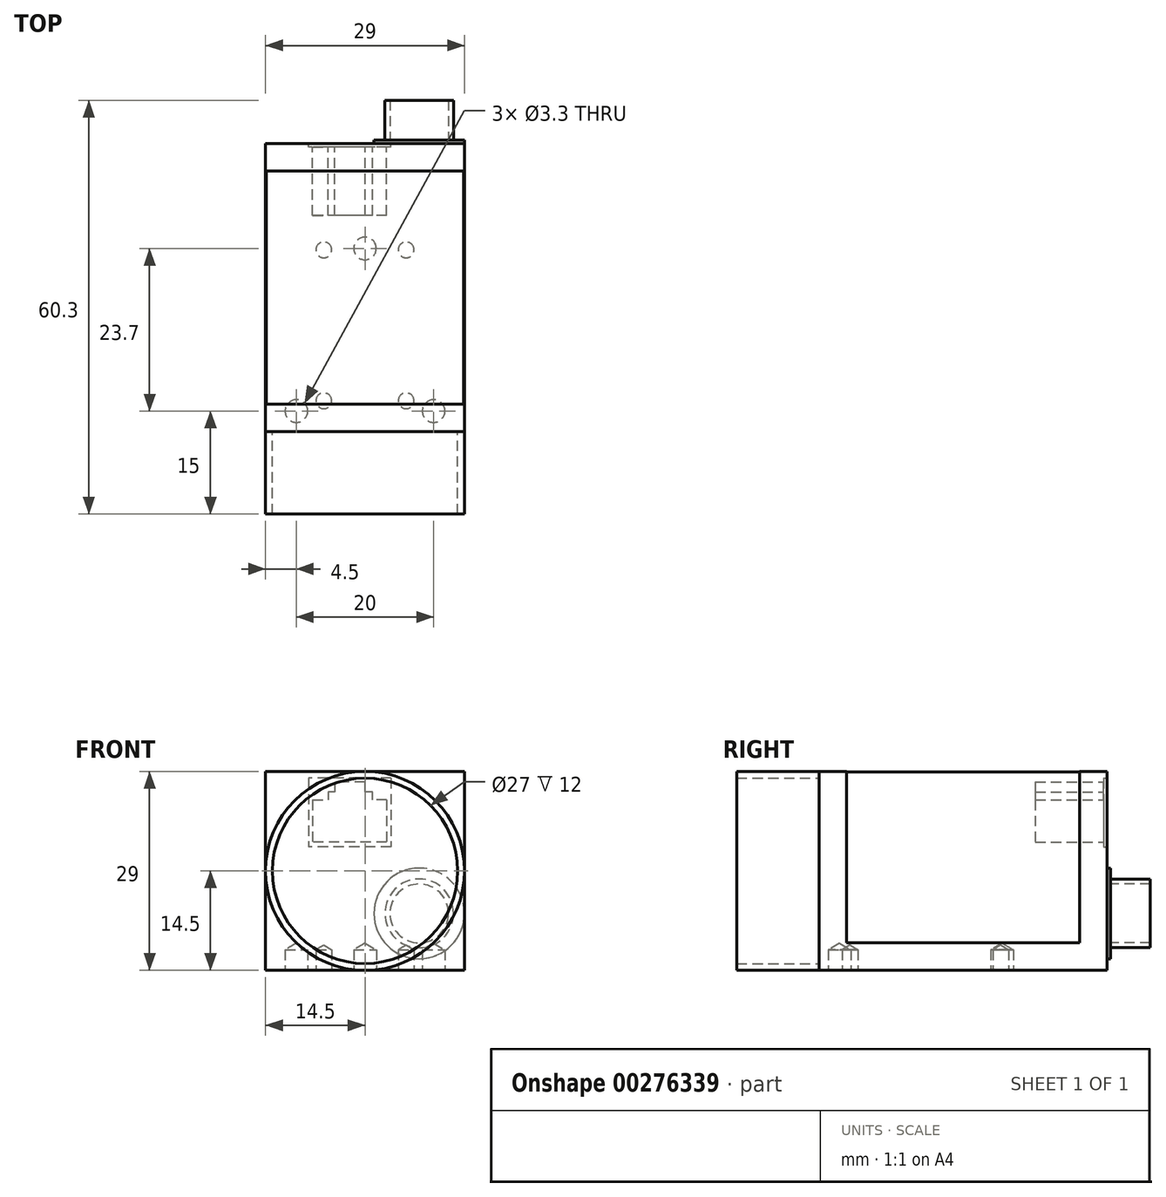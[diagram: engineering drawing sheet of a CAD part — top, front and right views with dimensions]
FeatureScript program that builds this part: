
annotation { "Feature Type Name" : "Feature", "Feature Type Description" : "" }
export const myFeature = defineFeature(function(context is Context, id is Id, definition is map)
    precondition{}
    {
        {
            var Q0;
            Q0=qCreatedBy(makeId("Front.planeOp"),FACE);
            var sketch = newSketch(context, id + "F0", { "sketchPlane" : qUnion([Q0])});
            skLineSegment(sketch, "E0.bottom", {"start": v(-14.5, 14.5) * mm, "end": v(14.5, 14.5) * mm});
            skLineSegment(sketch, "E0.top", {"start": v(-14.5, -14.5) * mm, "end": v(14.5, -14.5) * mm});
            skLineSegment(sketch, "E0.left", {"start": v(-14.5, 14.5) * mm, "end": v(-14.5, -14.5) * mm});
            skLineSegment(sketch, "E0.right", {"start": v(14.5, 14.5) * mm, "end": v(14.5, -14.5) * mm});
            skPoint(sketch, "E0.middle", {"position": v(0, 0) * mm});
            skSolve(sketch);
        }
        {
            var Q0;
            Q0 = qSketchRegion(id + "F0", true);
            extrude(context, id + "F1", {"entities" : qUnion([Q0]), "depth" : 42 * mm});
        }
        {
            var Q0;
            Q0=makeQuery(id+"F1.opExtrude","CAP_FACE",FACE,{"disambiguationData":[OSD([sQuery(id+"F0.wireOp",EDGE,"E0.bottom"),sQuery(id+"F0.wireOp",EDGE,"E0.top"),sQuery(id+"F0.wireOp",EDGE,"E0.left"),sQuery(id+"F0.wireOp",EDGE,"E0.right")])],"isStart":false});
            var sketch = newSketch(context, id + "F2", { "sketchPlane" : qUnion([Q0])});
            skCircle(sketch, "E1", {"center": v(0, 0) * mm, "radius": 14.5 * mm});
            skCircle(sketch, "E2", {"center": v(0, 0) * mm, "radius": 13.5 * mm});
            skSolve(sketch);
        }
        {
            var Q0;
            Q0 = qSketchRegion(id + "F2", true);
            extrude(context, id + "F3", {"entities" : qUnion([Q0]), "operationType" : NewBodyOperationType.ADD, "depth" : 12 * mm});
        }
        {
            var Q0;
            Q0=makeQuery(id+"F1.opExtrude","SWEPT_FACE",FACE,{"disambiguationData":[OSD([sQuery(id+"F0.wireOp",EDGE,"E0.right")])]});
            var sketch = newSketch(context, id + "F4", { "sketchPlane" : qUnion([Q0])});
            skLineSegment(sketch, "E3.bottom", {"start": v(-38, 14.5) * mm, "end": v(-4, 14.5) * mm});
            skLineSegment(sketch, "E3.top", {"start": v(-38, -10.5) * mm, "end": v(-4, -10.5) * mm});
            skLineSegment(sketch, "E3.left", {"start": v(-38, 14.5) * mm, "end": v(-38, -10.5) * mm});
            skLineSegment(sketch, "E3.right", {"start": v(-4, 14.5) * mm, "end": v(-4, -10.5) * mm});
            skSolve(sketch);
        }
        {
            var Q0;
            Q0 = qSketchRegion(id + "F4", true);
            extrude(context, id + "F5", {"entities" : qUnion([Q0]), "operationType" : NewBodyOperationType.REMOVE, "oppositeDirection" : true, "depth" : 0.1 * mm});
        }
        {
            var Q0;
            Q0=makeQuery(id+"F1.opExtrude","SWEPT_FACE",FACE,{"disambiguationData":[OSD([sQuery(id+"F0.wireOp",EDGE,"E0.left")])]});
            var sketch = newSketch(context, id + "F6", { "sketchPlane" : qUnion([Q0])});
            skLineSegment(sketch, "E4.bottom", {"start": v(4, -10.5) * mm, "end": v(38, -10.5) * mm});
            skLineSegment(sketch, "E4.top", {"start": v(4, 14.5) * mm, "end": v(38, 14.5) * mm});
            skLineSegment(sketch, "E4.left", {"start": v(4, -10.5) * mm, "end": v(4, 14.5) * mm});
            skLineSegment(sketch, "E4.right", {"start": v(38, -10.5) * mm, "end": v(38, 14.5) * mm});
            skSolve(sketch);
        }
        {
            var Q0;
            Q0=makeQuery(id+"F6.imprint","IMPRINT",FACE,{"disambiguationData":[TD([[makeQuery(id+"F6.imprint","IMPRINT",EDGE,{"derivedFrom":sQuery(id+"F6.wireOp",EDGE,"E4.bottom")}),1.0]])]});
            extrude(context, id + "F7", {"entities" : qUnion([Q0]), "operationType" : NewBodyOperationType.REMOVE, "oppositeDirection" : true, "depth" : 0.1 * mm});
        }
        {
            var Q0;
            Q0=makeQuery(id+"F1.opExtrude","SWEPT_FACE",FACE,{"disambiguationData":[OSD([sQuery(id+"F0.wireOp",EDGE,"E0.bottom")])]});
            var sketch = newSketch(context, id + "F8", { "sketchPlane" : qUnion([Q0])});
            skLineSegment(sketch, "E5.bottom", {"start": v(14.5, -4) * mm, "end": v(-14.4, -4) * mm});
            skLineSegment(sketch, "E5.top", {"start": v(14.5, -38) * mm, "end": v(-14.4, -38) * mm});
            skLineSegment(sketch, "E5.left", {"start": v(14.5, -4) * mm, "end": v(14.5, -38) * mm});
            skLineSegment(sketch, "E5.right", {"start": v(-14.4, -4) * mm, "end": v(-14.4, -38) * mm});
            skSolve(sketch);
        }
        {
            var Q0;
            Q0 = qSketchRegion(id + "F8", true);
            extrude(context, id + "F9", {"entities" : qUnion([Q0]), "operationType" : NewBodyOperationType.REMOVE, "oppositeDirection" : true, "depth" : 0.1 * mm});
        }
        {
            var Q0;
            Q0=makeQuery(id+"F1.opExtrude","SWEPT_FACE",FACE,{"disambiguationData":[OSD([sQuery(id+"F0.wireOp",EDGE,"E0.top")])]});
            var sketch = newSketch(context, id + "F10", { "sketchPlane" : qUnion([Q0])});
            skPoint(sketch, "E6", {"position": v(10, 39) * mm});
            skPoint(sketch, "E7", {"position": v(-10, 39) * mm});
            skPoint(sketch, "E8", {"position": v(0, 15.3) * mm});
            skSolve(sketch);
        }
        {
            var Q0;
            Q0=sQuery(id+"F10.wireOp",VERTEX,"E8");
            var Q1;
            Q1=sQuery(id+"F10.wireOp",VERTEX,"E6");
            var Q2;
            Q2=sQuery(id+"F10.wireOp",VERTEX,"E7");
            var Q3;
            Q3=makeQuery(id+"F1.opExtrude","SWEPT_BODY",BODY,{"disambiguationData":[OSD([sQuery(id+"F0.wireOp",EDGE,"E0.bottom"),sQuery(id+"F0.wireOp",EDGE,"E0.top"),sQuery(id+"F0.wireOp",EDGE,"E0.left"),sQuery(id+"F0.wireOp",EDGE,"E0.right")])]});
            hole(context, id + "F11", {"style" : HoleStyle.SIMPLE, "endStyle" : HoleEndStyle.BLIND, "standardTappedOrClearance" : lookupTablePath({ "standard" : "ISO", "fit" : "Normal", "size" : "M3", "type" : "Clearance" }), "standardBlindInLast" : lookupTablePath({ "fit" : "Standard", "standard" : "ISO", "size" : "M3", "type" : "Clearance" }), "holeDiameter" : 3.3 * mm, "holeDepth" : 3 * mm, "tappedDepth" : 12 * mm, "tapClearance" : 3, "locations" : qUnion([Q0, Q1, Q2]), "scope" : qUnion([Q3])});
        }
        {
            var Q0;
            Q0=makeQuery(id+"F1.opExtrude","SWEPT_FACE",FACE,{"disambiguationData":[OSD([sQuery(id+"F0.wireOp",EDGE,"E0.top")])]});
            var sketch = newSketch(context, id + "F12", { "sketchPlane" : qUnion([Q0])});
            skPoint(sketch, "E9", {"position": v(6, 15.5) * mm});
            skPoint(sketch, "E10", {"position": v(-6, 15.5) * mm});
            skPoint(sketch, "E11", {"position": v(6, 37.5) * mm});
            skPoint(sketch, "E12", {"position": v(-6, 37.5) * mm});
            skSolve(sketch);
        }
        {
            var Q0;
            Q0=sQuery(id+"F12.wireOp",VERTEX,"E9");
            var Q1;
            Q1=sQuery(id+"F12.wireOp",VERTEX,"E10");
            var Q2;
            Q2=sQuery(id+"F12.wireOp",VERTEX,"E11");
            var Q3;
            Q3=sQuery(id+"F12.wireOp",VERTEX,"E12");
            var Q4;
            Q4=makeQuery(id+"F1.opExtrude","SWEPT_BODY",BODY,{"disambiguationData":[OSD([sQuery(id+"F0.wireOp",EDGE,"E0.bottom"),sQuery(id+"F0.wireOp",EDGE,"E0.top"),sQuery(id+"F0.wireOp",EDGE,"E0.left"),sQuery(id+"F0.wireOp",EDGE,"E0.right")])]});
            hole(context, id + "F13", {"style" : HoleStyle.SIMPLE, "endStyle" : HoleEndStyle.BLIND, "holeDiameter" : 2.3 * mm, "holeDepth" : 3 * mm, "tappedDepth" : 12 * mm, "tapClearance" : 3, "locations" : qUnion([Q0, Q1, Q2, Q3]), "scope" : qUnion([Q4])});
        }
        {
            var Q0;
            Q0=makeQuery(id+"F1.opExtrude","CAP_FACE",FACE,{"disambiguationData":[OSD([sQuery(id+"F0.wireOp",EDGE,"E0.bottom"),sQuery(id+"F0.wireOp",EDGE,"E0.top"),sQuery(id+"F0.wireOp",EDGE,"E0.left"),sQuery(id+"F0.wireOp",EDGE,"E0.right")])],"isStart":true});
            var sketch = newSketch(context, id + "F14", { "sketchPlane" : qUnion([Q0])});
            skCircle(sketch, "E13", {"center": v(-7.9, -6.2) * mm, "radius": 6.6 * mm});
            skSolve(sketch);
        }
        {
            var Q0;
            Q0 = qSketchRegion(id + "F14", true);
            extrude(context, id + "F15", {"entities" : qUnion([Q0]), "operationType" : NewBodyOperationType.ADD, "depth" : 0.5 * mm});
        }
        {
            var Q0;
            Q0=makeQuery(id+"F1.opExtrude","CAP_FACE",FACE,{"disambiguationData":[OSD([sQuery(id+"F0.wireOp",EDGE,"E0.bottom"),sQuery(id+"F0.wireOp",EDGE,"E0.top"),sQuery(id+"F0.wireOp",EDGE,"E0.left"),sQuery(id+"F0.wireOp",EDGE,"E0.right")])],"isStart":true});
            var sketch = newSketch(context, id + "F16", { "sketchPlane" : qUnion([Q0])});
            skLineSegment(sketch, "E14.bottom", {"start": v(-3.8, 13.5) * mm, "end": v(8.2, 13.5) * mm});
            skLineSegment(sketch, "E14.top", {"start": v(-3.8, 3.5) * mm, "end": v(8.2, 3.5) * mm});
            skLineSegment(sketch, "E14.left", {"start": v(-3.8, 13.5) * mm, "end": v(-3.8, 3.5) * mm});
            skLineSegment(sketch, "E14.right", {"start": v(8.2, 13.5) * mm, "end": v(8.2, 3.5) * mm});
            skSolve(sketch);
        }
        {
            var Q0;
            Q0=makeQuery(id+"F16.imprint","IMPRINT",FACE,{"disambiguationData":[TD([[makeQuery(id+"F16.imprint","IMPRINT",EDGE,{"derivedFrom":sQuery(id+"F16.wireOp",EDGE,"E14.bottom")}),-1.0]])]});
            extrude(context, id + "F17", {"entities" : qUnion([Q0]), "operationType" : NewBodyOperationType.REMOVE, "oppositeDirection" : true, "depth" : 0.5 * mm});
        }
        {
            var Q0;
            Q0=makeQuery(id+"F17.boolean.opBoolean","COPY",FACE,{"derivedFrom":makeQuery(id+"F17.opExtrude","CAP_FACE",FACE,{"disambiguationData":[OSD([sQuery(id+"F16.wireOp",EDGE,"E14.bottom"),sQuery(id+"F16.wireOp",EDGE,"E14.top"),sQuery(id+"F16.wireOp",EDGE,"E14.left"),sQuery(id+"F16.wireOp",EDGE,"E14.right")])],"isStart":false})});
            var sketch = newSketch(context, id + "F18", { "sketchPlane" : qUnion([Q0])});
            skLineSegment(sketch, "E15.top", {"start": v(-3.15, 4.18) * mm, "end": v(7.66, 4.18) * mm});
            skLineSegment(sketch, "E15.left", {"start": v(-3.15, 10.33) * mm, "end": v(-3.15, 4.18) * mm});
            skLineSegment(sketch, "E15.right", {"start": v(7.66, 10.33) * mm, "end": v(7.66, 4.18) * mm});
            skLineSegment(sketch, "E16", {"start": v(-3.15, 10.33) * mm, "end": v(-1.1, 10.33) * mm});
            skLineSegment(sketch, "E17", {"start": v(-1.1, 10.33) * mm, "end": v(-1.1, 11.52) * mm});
            skLineSegment(sketch, "E18", {"start": v(-1.1, 11.52) * mm, "end": v(0, 11.52) * mm});
            skLineSegment(sketch, "E19", {"start": v(0, 11.52) * mm, "end": v(0, 12.93) * mm});
            skLineSegment(sketch, "E20", {"start": v(0, 12.93) * mm, "end": v(4.39, 12.93) * mm});
            skLineSegment(sketch, "E21", {"start": v(4.39, 12.93) * mm, "end": v(4.39, 11.52) * mm});
            skLineSegment(sketch, "E22", {"start": v(4.39, 11.52) * mm, "end": v(5.34, 11.52) * mm});
            skLineSegment(sketch, "E23", {"start": v(5.34, 11.52) * mm, "end": v(5.34, 10.33) * mm});
            skLineSegment(sketch, "E24", {"start": v(7.66, 10.33) * mm, "end": v(5.34, 10.33) * mm});
            skSolve(sketch);
        }
        {
            var Q0;
            Q0=makeQuery(id+"F18.imprint","IMPRINT",FACE,{"disambiguationData":[TD([[makeQuery(id+"F18.imprint","IMPRINT",EDGE,{"derivedFrom":sQuery(id+"F18.wireOp",EDGE,"E15.top")}),1.0]])]});
            extrude(context, id + "F19", {"entities" : qUnion([Q0]), "operationType" : NewBodyOperationType.REMOVE, "oppositeDirection" : true, "depth" : 10 * mm});
        }
        {
            var Q0;
            Q0=makeQuery(id+"F15.opExtrude","CAP_FACE",FACE,{"disambiguationData":[OSD([sQuery(id+"F14.wireOp",EDGE,"E13")])],"isStart":false});
            var sketch = newSketch(context, id + "F20", { "sketchPlane" : qUnion([Q0])});
            skCircle(sketch, "E25", {"center": v(-7.9, -6.2) * mm, "radius": 5 * mm});
            skCircle(sketch, "E26", {"center": v(-7.9, -6.2) * mm, "radius": 4.28 * mm});
            skSolve(sketch);
        }
        {
            var Q0;
            Q0 = qSketchRegion(id + "F20", true);
            extrude(context, id + "F21", {"entities" : qUnion([Q0]), "operationType" : NewBodyOperationType.ADD, "depth" : 5.8 * mm});
        }
    });
